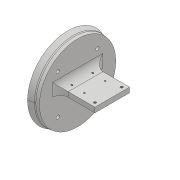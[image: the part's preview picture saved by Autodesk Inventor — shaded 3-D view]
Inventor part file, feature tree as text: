
AUTODESK INVENTOR PART (.ipt)
format: ipt  version: 2018 (Build 220112000, 112)  size: 477,696 bytes
history: native  units: mm
features: sketch x14, fillet x9, extrude x8, projected_geometry x5, hole x4, revolve x2, plane x2, shell x1, pattern_circular x1
ambient origin geometry x8: Origin, YZ Plane, XZ Plane, XY Plane, X Axis, Y Axis, Z Axis, Center Point
bodies: Solid1 (feature_tree), Solid3 (feature_tree)
feature tree (46):
  revolve  "Revolution1"  [1 undecoded]
  fillet  "Fillet1"  Radius=45.0mm
  shell  "Shell1"  Thickness=45.0mm
  fillet  "Fillet3"  Radius=10.0mm
  plane  "Work Plane1"
  extrude  "Extrusion1"  Depth=22.0mm
  hole  "Hole1"  [1 undecoded]
  extrude  "Extrusion3"  Depth=25.0mm
  fillet  "Fillet4"  Radius=1.0mm
  pattern_circular  "Circular Pattern1"  Count=5  [1 undecoded]
  extrude  "Extrusion4"  Depth=10.0mm
  fillet  "Fillet5"  Radius=10.0mm
  fillet  "Fillet6"  Radius=8.0mm
  fillet  "Fillet7"  Radius=30.0mm
  fillet  "Fillet8"  Radius=8.0mm
  plane  "Work Plane2"
  extrude  "Extrusion5"  TaperAngle=0.0deg  [1 undecoded]
  extrude  "Extrusion6"  Depth=60.0mm TaperAngle=360.0deg
  revolve  "Revolution2"  [1 undecoded]
  extrude  "Extrusion7"  Depth=8.0mm
  hole  "Hole2"  [1 undecoded]
  extrude  "Extrusion8"  Depth=10.0mm TaperAngle=0.0deg
  fillet  "Fillet9"  [1 undecoded]
  extrude  "Extrusion9"  TaperAngle=0.0deg  [1 undecoded]
  fillet  "Fillet10"  Radius=40.0mm
  hole  "Hole3"  [1 undecoded]
  hole  "Hole4"  [1 undecoded]
  sketch  "Sketch1"  dims[d0=125.0mm d1=40.0mm d2=45.0mm d3=45.0mm d4=10.0mm]
  sketch  "Sketch2"  dims[d5=70.0mm d6=22.0mm]
  sketch  "Sketch4"  dims[d7=70.0mm d8=90.0deg]
  projected_geometry  "Projected Loop2"
  sketch  "Sketch5"  dims[d9=17.104227mm d10=25.0mm d12=1.0mm]
  sketch  "Sketch6"  dims[d13=0.25mm d14=50.0mm]
  projected_geometry  "Projected Loop3"
  sketch  "Sketch7"  dims[d15=15.0mm d16=38.0mm d17=10.0mm d18=0.0mm d22=8.0mm]
  sketch  "Sketch10"  dims[d23=3.2mm d24=6.0mm d25=6.3mm d26=2.0mm d27=90.0deg d28=15.0mm d29=20.594885mm d30=30.0mm d31=8.0mm]
  sketch  "Sketch11"  dims[d32=40.0mm d33=0.0mm d34=0.0mm]
  projected_geometry  "Projected Loop4"
  sketch  "Sketch12"  dims[d35=2.0mm d36=60.0mm d37=360.0deg]
  sketch  "Sketch13"  dims[d39=20.0mm d40=10.0mm d41=0.0mm]
  sketch  "Sketch14"  dims[d42=8.0mm d43=8.0mm]
  sketch  "Sketch15"  dims[d44=3.0mm d45=3.5mm]
  projected_geometry  "Projected Loop5"
  sketch  "Sketch16"  dims[d46=50.0mm d47=10.0mm d48=0.0mm d49=0.0mm d50=0.0mm]
  sketch  "Sketch17"  dims[d51=90.0deg d52=0.0mm d53=0.0mm d54=40.0mm d55=40.0mm d56=3.4mm d57=10.0mm d58=4.0mm d59=2.0mm d60=90.0deg d61=8.0mm d62=20.594885mm d63=5.0mm d64=25.0mm d65=10.0mm d66=0.0mm d67=2.0mm d68=5.0mm d69=35.0mm d70=35.0mm d71=0.0mm d72=8.0mm d73=12.5mm d74=21.0mm d75=24.0mm d76=1.567mm d77=10.0mm d78=4.0mm d79=2.0mm d80=90.0deg d81=6.3mm d82=20.594885mm d83=27.0mm d84=4.0mm d85=2.459mm d86=6.0mm d87=4.0mm d88=2.0mm d89=90.0deg d90=8.8mm d91=20.594885mm]
  projected_geometry  "Project Cut Edges1"
note: 10 required parameter values undecoded (feature->parameter linkage not recoverable at this tier; creation-order binding heuristic only, values carry confidence <= 0.55)